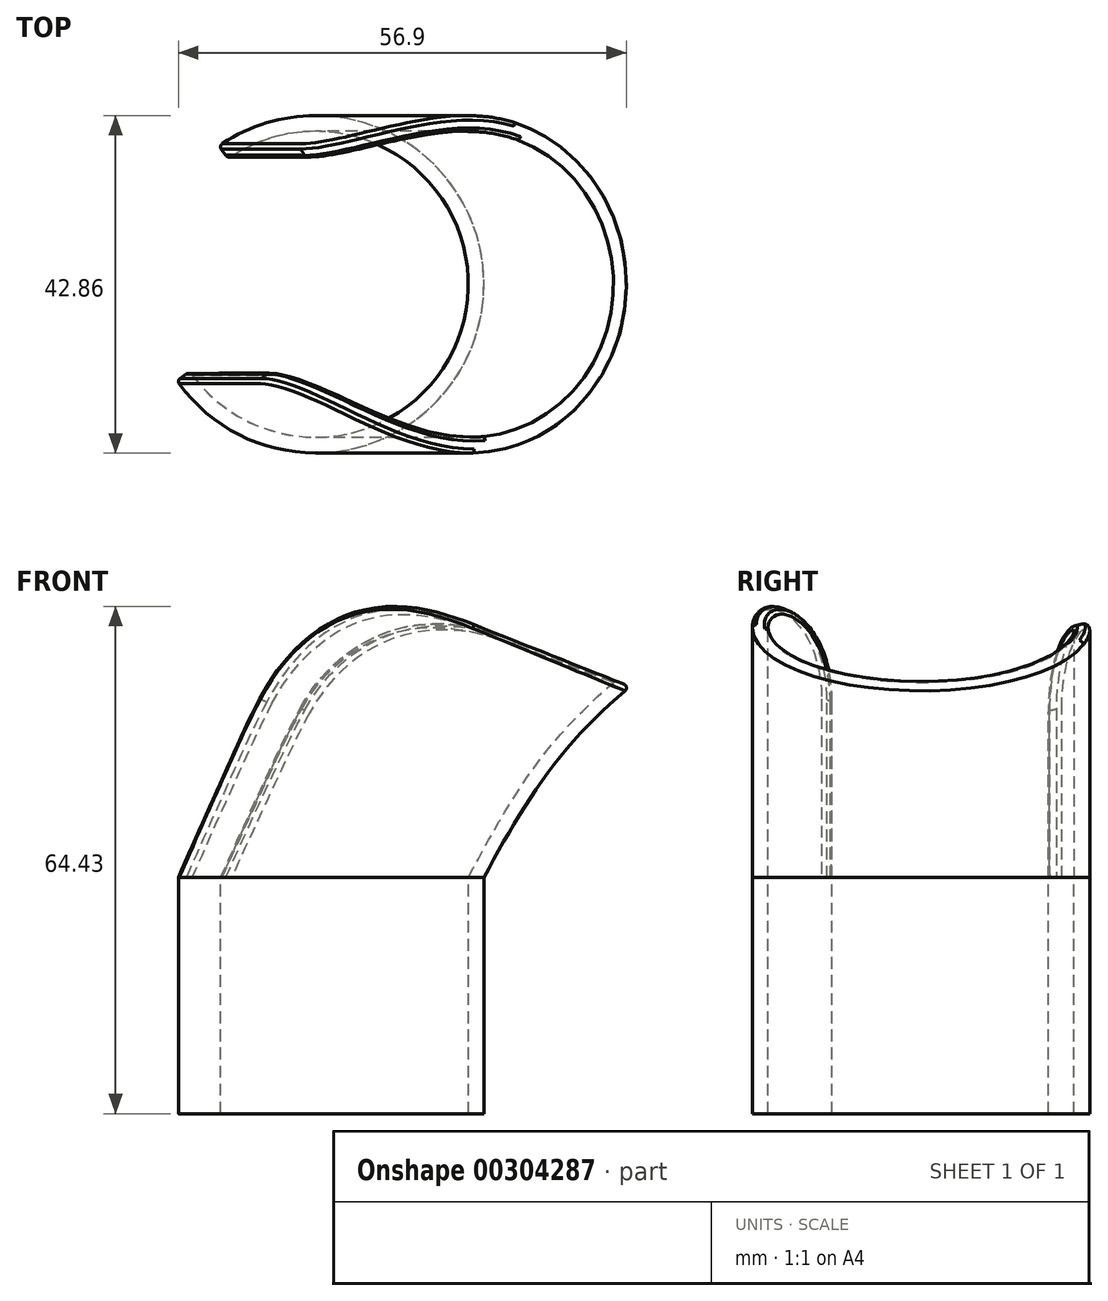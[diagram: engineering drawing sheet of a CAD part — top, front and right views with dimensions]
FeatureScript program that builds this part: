
annotation { "Feature Type Name" : "Feature", "Feature Type Description" : "" }
export const myFeature = defineFeature(function(context is Context, id is Id, definition is map)
    precondition{}
    {
        {
            var Q0;
            Q0=qCreatedBy(makeId("Top.planeOp"),FACE);
            var sketch = newSketch(context, id + "F0", { "sketchPlane" : qUnion([Q0])});
            skArc(sketch, "E0", {"start": v(-15.95, -11.1) * mm, "mid": v(19.12, -3.43) * mm, "end": v(-11.1, 15.95) * mm});
            skArc(sketch, "E1.0", {"start": v(-17.59, -12.24) * mm, "mid": v(21.09, -3.79) * mm, "end": v(-12.24, 17.59) * mm});
            skLineSegment(sketch, "E2", {"start": v(-11.1, 15.95) * mm, "end": v(-12.24, 17.59) * mm});
            skLineSegment(sketch, "E3", {"start": v(-15.95, -11.1) * mm, "end": v(-17.59, -12.24) * mm});
            skSolve(sketch);
        }
        {
            var Q0;
            Q0=qCreatedBy(makeId("Front.planeOp"),FACE);
            var sketch = newSketch(context, id + "F1", { "sketchPlane" : qUnion([Q0])});
            skFitSpline(sketch, "E4", {"points": [v(21.6, 0) * mm, v(28.43, 11.53) * mm, v(40.13, 24.19) * mm], "startDerivative": vector(9.41, 17.71) * mm, "endDerivative": vector(29.15, 24.75) * mm});
            skSolve(sketch);
        }
        {
            var Q0;
            Q0=makeQuery(id+"F0.imprint","IMPRINT",FACE,{"disambiguationData":[TD([[makeQuery(id+"F0.imprint","IMPRINT",EDGE,{"derivedFrom":sQuery(id+"F0.wireOp",EDGE,"E0")}),-1.0]])]});
            var Q1;
            Q1=sQuery(id+"F1.wireOp",EDGE,"E4");
            sweep(context, id + "F2", {"profiles" : qUnion([Q0]), "path" : qUnion([Q1])});
        }
        {
            var Q0;
            Q0=makeQuery(id+"F2.opSweep","CAP_EDGE",EDGE,{"disambiguationData":[OSD([sQuery(id+"F0.wireOp",EDGE,"E3"),sQuery(id+"F1.wireOp",VERTEX,"E4.end")])],"isStart":false});
            fillet(context, id + "F3", {"entities" : qUnion([Q0]), "radius" : 20 * mm, "tangentPropagation" : true, "allowEdgeOverflow" : false});
        }
        {
            var Q0;
            Q0=makeQuery(id+"F2.opSweep","CAP_EDGE",EDGE,{"disambiguationData":[OSD([sQuery(id+"F0.wireOp",EDGE,"E2"),sQuery(id+"F1.wireOp",VERTEX,"E4.end")])],"isStart":false});
            fillet(context, id + "F4", {"entities" : qUnion([Q0]), "radius" : 20 * mm, "tangentPropagation" : true, "allowEdgeOverflow" : false});
        }
        {
            var Q0;
            Q0=makeQuery(id+"F2.opSweep","CAP_EDGE",EDGE,{"disambiguationData":[OSD([sQuery(id+"F0.wireOp",EDGE,"E1.0"),sQuery(id+"F1.wireOp",VERTEX,"E4.end")])],"isStart":false});
            fillet(context, id + "F5", {"entities" : qUnion([Q0]), "radius" : 0.5 * mm, "tangentPropagation" : true, "allowEdgeOverflow" : false});
        }
        {
            var Q0;
            Q0=makeQuery(id+"F2.opSweep","CAP_EDGE",EDGE,{"disambiguationData":[OSD([sQuery(id+"F0.wireOp",EDGE,"E0"),sQuery(id+"F1.wireOp",VERTEX,"E4.end")])],"isStart":false});
            fillet(context, id + "F6", {"entities" : qUnion([Q0]), "radius" : 0.5 * mm, "tangentPropagation" : true, "allowEdgeOverflow" : false});
        }
        {
            var Q0;
            Q0=makeQuery(id+"F2.opSweep","CAP_FACE",FACE,{"disambiguationData":[OSD([sQuery(id+"F0.wireOp",EDGE,"E0"),sQuery(id+"F0.wireOp",EDGE,"E1.0"),sQuery(id+"F0.wireOp",EDGE,"E2"),sQuery(id+"F0.wireOp",EDGE,"E3"),sQuery(id+"F1.wireOp",VERTEX,"E4.start")])],"isStart":true});
            extrude(context, id + "F7", {"entities" : qUnion([Q0]), "operationType" : NewBodyOperationType.ADD, "depth" : 30 * mm});
        }
    });
